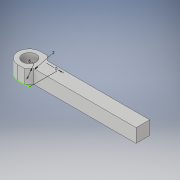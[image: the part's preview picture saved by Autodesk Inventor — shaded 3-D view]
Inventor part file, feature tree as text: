
AUTODESK INVENTOR PART (.ipt)
format: ipt  version: 2019 (Build 230136000, 136)  size: 155,648 bytes
history: native  units: mm
features: extrude x4, sketch x2, chamfer x1
ambient origin geometry x8: Origin, YZ Plane, XZ Plane, XY Plane, X Axis, Y Axis, Z Axis, Center Point
bodies: Solid1 (feature_tree)
feature tree (7):
  sketch  "Sketch1"  dims[d0=6.0mm d1=2.0mm]
  extrude  "Extrusion1"  Depth=2.0mm
  extrude  "Extrusion2"  Depth=6.0mm TaperAngle=0.0deg
  extrude  "Extrusion3"  Depth=6.0mm TaperAngle=0.0deg
  extrude  "Extrusion4"  TaperAngle=0.0deg  [1 undecoded]
  chamfer  "Chamfer1"  Distance=2.0mm
  sketch  "Sketch2"  dims[d2=6.0mm d3=0.0mm d4=6.0mm d5=0.0mm d6=6.0mm d7=0.0mm d8=0.0mm d9=2.0mm d10=2.0mm d11=45.0mm d12=0.0mm d13=2.0mm d14=2.0mm d15=45.0deg]
note: 1 required parameter value undecoded (feature->parameter linkage not recoverable at this tier; creation-order binding heuristic only, values carry confidence <= 0.55)
